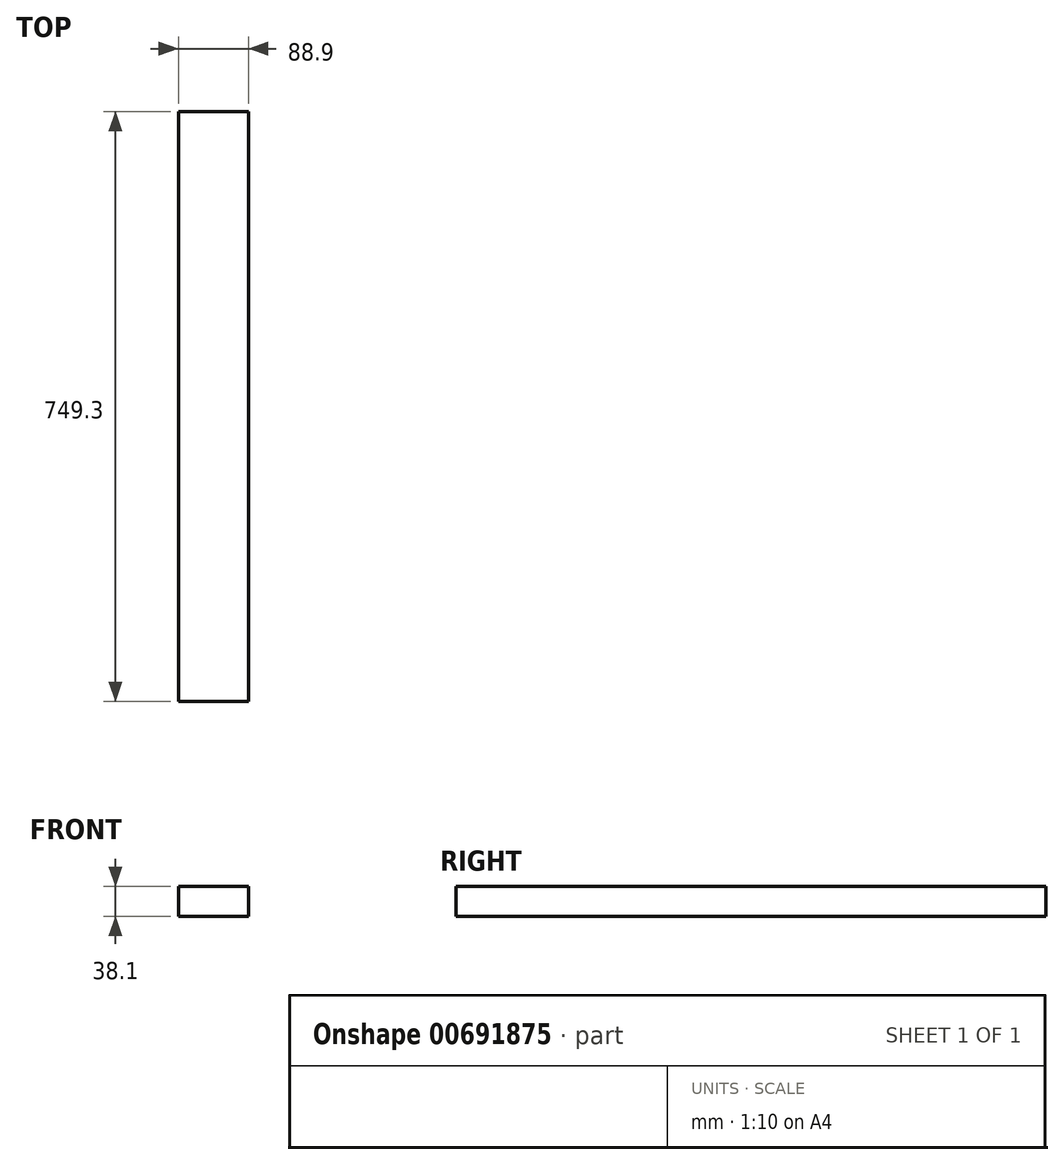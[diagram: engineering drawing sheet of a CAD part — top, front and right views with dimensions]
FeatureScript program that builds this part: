
annotation { "Feature Type Name" : "Feature", "Feature Type Description" : "" }
export const myFeature = defineFeature(function(context is Context, id is Id, definition is map)
    precondition{}
    {
        {
            var Q0;
            Q0=qCreatedBy(makeId("Front.planeOp"),FACE);
            var sketch = newSketch(context, id + "F0", { "sketchPlane" : qUnion([Q0])});
            skLineSegment(sketch, "E0.bottom", {"start": v(0, 0) * mm, "end": v(88.9, 0) * mm});
            skLineSegment(sketch, "E0.top", {"start": v(0, 38.1) * mm, "end": v(88.9, 38.1) * mm});
            skLineSegment(sketch, "E0.left", {"start": v(0, 0) * mm, "end": v(0, 38.1) * mm});
            skLineSegment(sketch, "E0.right", {"start": v(88.9, 0) * mm, "end": v(88.9, 38.1) * mm});
            skSolve(sketch);
        }
        {
            var Q0;
            Q0=makeQuery(id+"F0.imprint","IMPRINT",FACE,{"disambiguationData":[TD([[makeQuery(id+"F0.imprint","IMPRINT",EDGE,{"derivedFrom":sQuery(id+"F0.wireOp",EDGE,"E0.bottom")}),1.0]])]});
            extrude(context, id + "F1", {"entities" : qUnion([Q0]), "depth" : 749.3 * mm, "offsetDistance" : 25.4 * mm});
        }
    });
